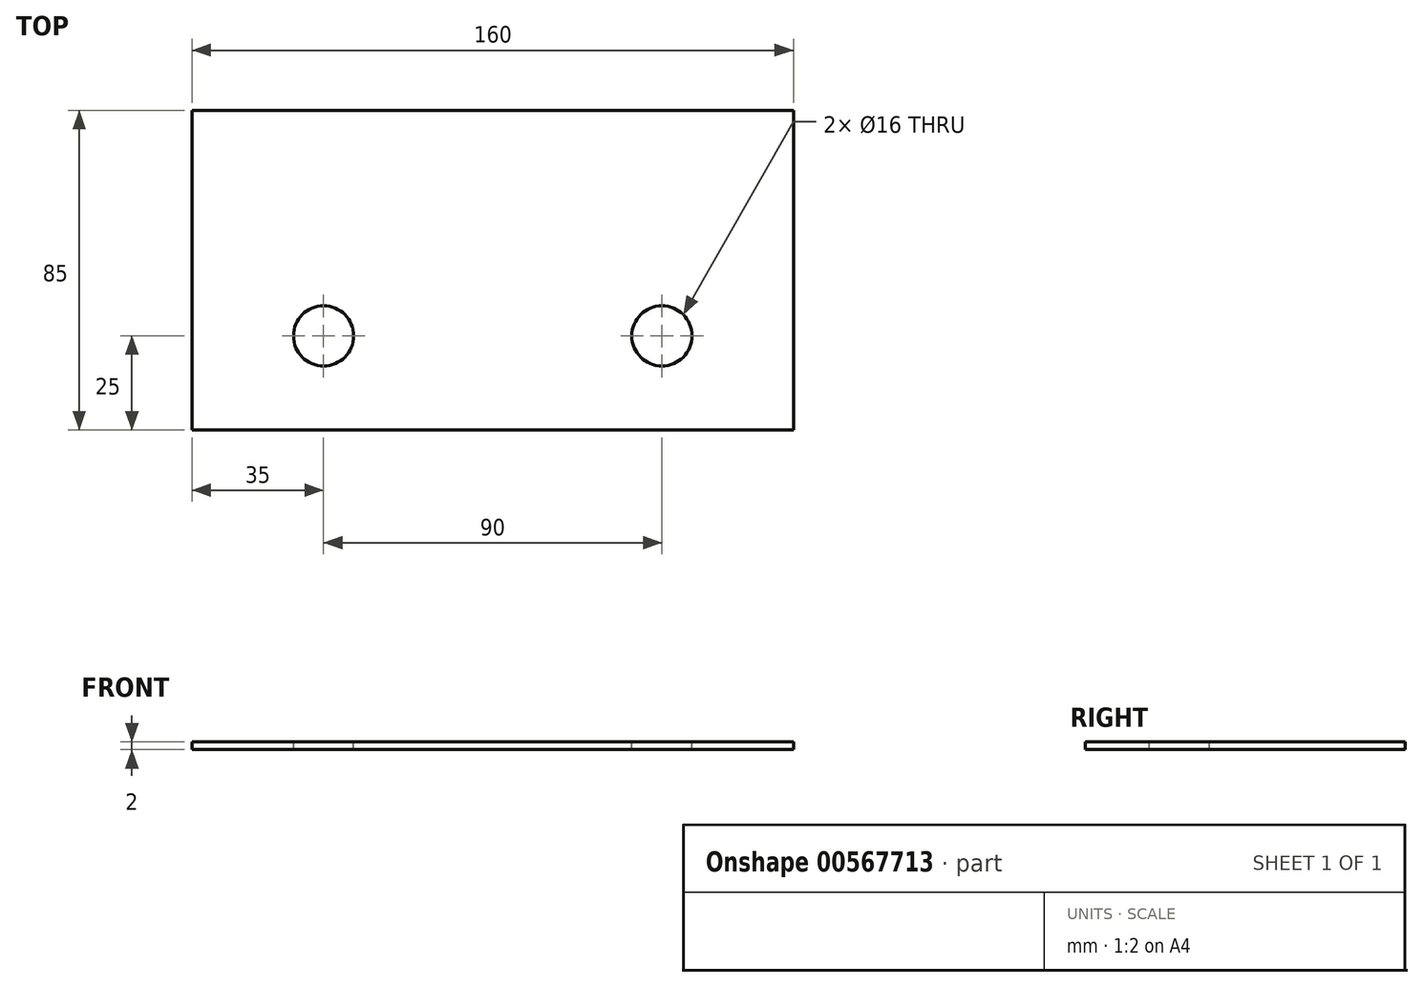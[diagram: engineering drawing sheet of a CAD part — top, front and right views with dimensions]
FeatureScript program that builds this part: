
annotation { "Feature Type Name" : "Feature", "Feature Type Description" : "" }
export const myFeature = defineFeature(function(context is Context, id is Id, definition is map)
    precondition{}
    {
        {
            var Q0;
            Q0=qCreatedBy(makeId("Top.planeOp"),FACE);
            var sketch = newSketch(context, id + "F0", { "sketchPlane" : qUnion([Q0])});
            skLineSegment(sketch, "E0.bottom", {"start": v(80, -42.5) * mm, "end": v(-80, -42.5) * mm});
            skLineSegment(sketch, "E0.top", {"start": v(80, 42.5) * mm, "end": v(-80, 42.5) * mm});
            skLineSegment(sketch, "E0.left", {"start": v(80, -42.5) * mm, "end": v(80, 42.5) * mm});
            skLineSegment(sketch, "E0.right", {"start": v(-80, -42.5) * mm, "end": v(-80, 42.5) * mm});
            skPoint(sketch, "E0.middle", {"position": v(0, 0) * mm});
            skCircle(sketch, "E1", {"center": v(-45, -17.5) * mm, "radius": 8 * mm});
            skCircle(sketch, "E2", {"center": v(45, -17.5) * mm, "radius": 8 * mm});
            skSolve(sketch);
        }
        {
            var Q0;
            Q0 = qSketchRegion(id + "F0", true);
            extrude(context, id + "F1", {"entities" : qUnion([Q0]), "oppositeDirection" : true, "depth" : 2 * mm, "offsetDistance" : 25 * mm});
        }
    });
